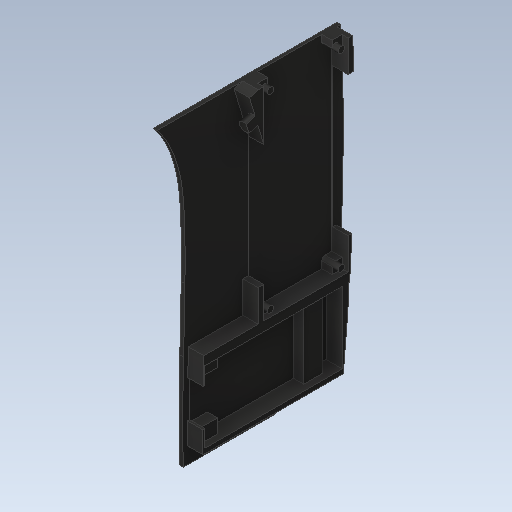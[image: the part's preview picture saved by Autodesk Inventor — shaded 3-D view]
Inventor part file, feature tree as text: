
AUTODESK INVENTOR PART (.ipt)
format: ipt  version: 2020.1 (Build 241239000, 239)  size: 1,689,088 bytes
history: native  units: mm
features: extrude x9, sketch x7, other x4, projected_geometry x3, split x1, chamfer x1, surface_op x1
ambient origin geometry x8: Origin, YZ Plane, XZ Plane, XY Plane, X Axis, Y Axis, Z Axis, Center Point
bodies: Solid1 (feature_tree)
feature tree (26):
  other  "Remote Bottom Shell.ipt"
  sketch  "Sketch1"  dims[d0=10.0mm d1=18.1mm]
  extrude  "Extrusion2"  Depth=10.0mm
  extrude  "Extrusion4"  Depth=29.5mm
  sketch  "Sketch3"  dims[d2=43.6mm d5=29.5mm]
  extrude  "Extrusion5"  Depth=2.0mm
  extrude  "Extrusion6"  Depth=1.2mm
  extrude  "Extrusion7"  Depth=1.2mm
  split  "Split1"
  extrude  "Extrusion8"  Depth=1.4mm
  extrude  "Extrusion9"  Depth=10.0mm
  extrude  "Extrusion10"  Depth=10.0mm TaperAngle=0.0deg
  chamfer  "Chamfer1"  Distance=3.5mm
  extrude  "Extrusion11"  Depth=10.0mm
  other  "Plate Solid::Remote Bottom Shell.ipt"
  other  "TaggingFeature1"
  projected_geometry  "Projected Loop1"
  sketch  "Sketch4"  dims[d6=15.35mm d7=2.0mm]
  sketch  "Sketch5"  dims[d8=0.2mm d9=0.0mm d17=1.2mm]
  projected_geometry  "Projected Loop2"
  projected_geometry  "Projected Loop3"
  sketch  "Sketch6"  dims[d18=1.2mm d21=30.0mm]
  sketch  "Sketch7"  dims[d22=3.3mm d23=0.0mm d26=1.4mm]
  sketch  "Sketch8"  dims[d27=15.22mm d28=40.66mm d29=2.2mm d30=0.0mm d31=3.5mm d32=0.0mm d33=4.0mm d34=3.0mm d43=2.2mm d44=0.0mm d45=4.0mm d46=3.0mm d47=0.8mm d48=10.0mm d49=0.0mm d51=2.904437mm d52=10.0mm d53=0.0mm d54=0.3mm d55=0.3mm d56=10.0mm d57=0.0mm d58=4.0mm d59=0.3mm d60=45.0deg d61=8.0mm d62=1.3mm d63=0.2mm d64=8.0mm d65=2.4mm d67=2.0mm d68=0.0mm d70=5.5mm d73=1.5mm]
  surface_op  "Surface1"
  other  "Srf1"
